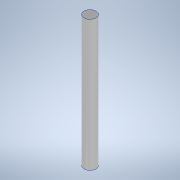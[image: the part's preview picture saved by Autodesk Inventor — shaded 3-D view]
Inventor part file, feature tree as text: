
AUTODESK INVENTOR PART (.ipt)
format: ipt  version: 2020.3 (Build 243373000, 373)  size: 90,112 bytes
history: native  units: mm
features: other x1, extrude x1, sketch x1
ambient origin geometry x8: Origin, YZ Plane, XZ Plane, XY Plane, X Axis, Y Axis, Z Axis, Center Point
bodies: Body1 (feature_tree)
feature tree (3):
  other  "ソリッド1"
  extrude  "押し出し1"  Depth=6.0mm
  sketch  "スケッチ1"
